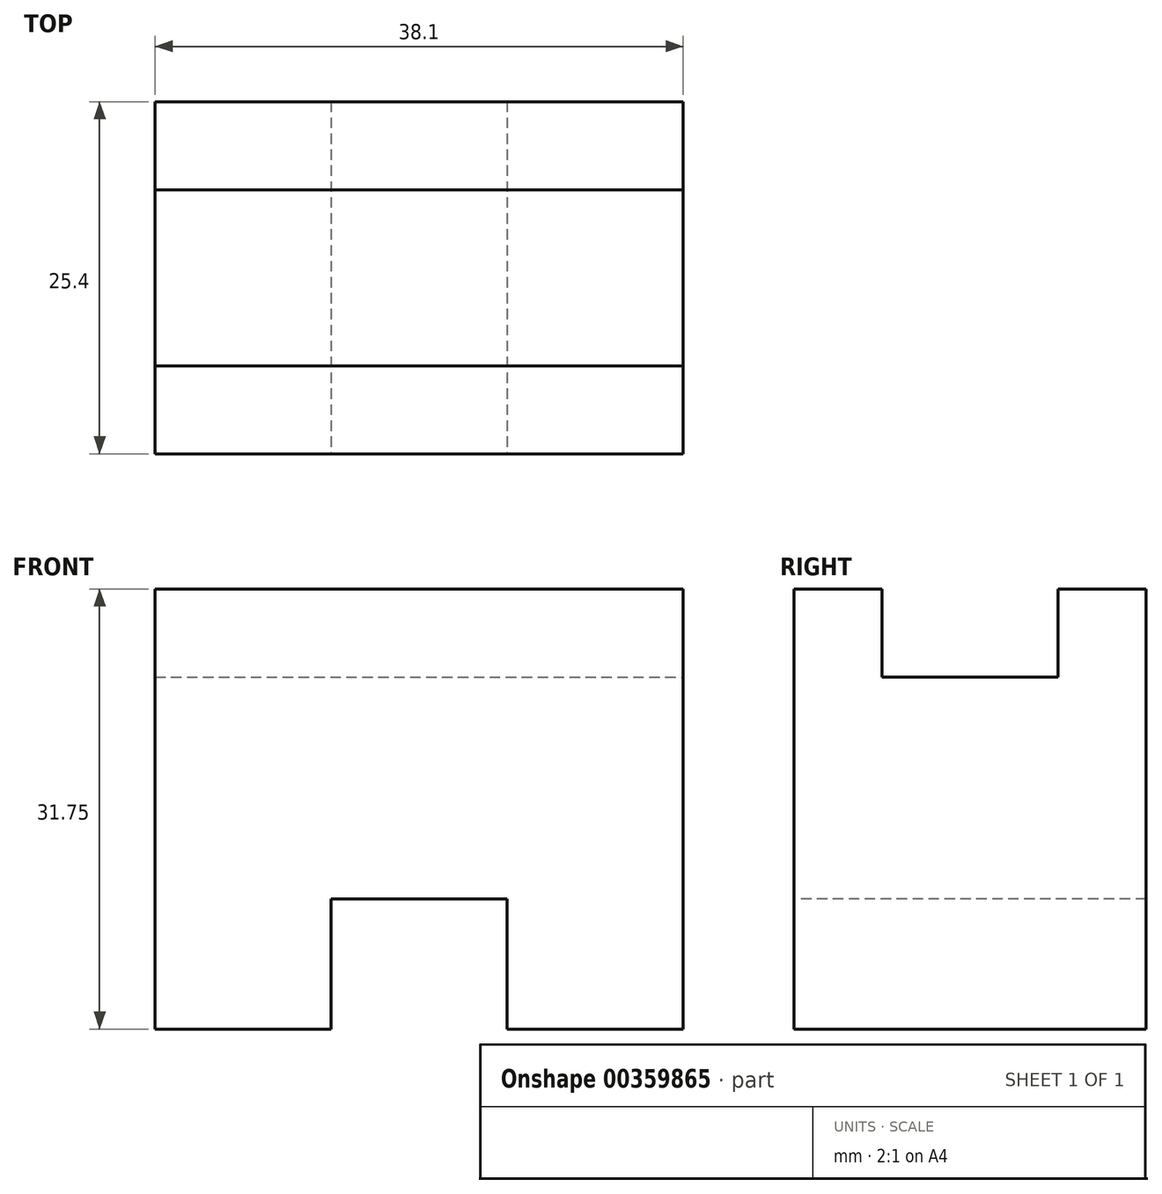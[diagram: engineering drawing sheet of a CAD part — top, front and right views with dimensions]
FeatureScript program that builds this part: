
annotation { "Feature Type Name" : "Feature", "Feature Type Description" : "" }
export const myFeature = defineFeature(function(context is Context, id is Id, definition is map)
    precondition{}
    {
        {
            var Q0;
            Q0=qCreatedBy(makeId("Front.planeOp"),FACE);
            var sketch = newSketch(context, id + "F0", { "sketchPlane" : qUnion([Q0])});
            skLineSegment(sketch, "E0", {"start": v(0, 0) * mm, "end": v(12.7, 0) * mm});
            skLineSegment(sketch, "E1", {"start": v(12.7, 0) * mm, "end": v(12.7, 9.4) * mm});
            skLineSegment(sketch, "E2", {"start": v(12.7, 9.4) * mm, "end": v(25.4, 9.4) * mm});
            skLineSegment(sketch, "E3", {"start": v(25.4, 9.4) * mm, "end": v(25.4, 0) * mm});
            skLineSegment(sketch, "E4", {"start": v(25.4, 0) * mm, "end": v(38.1, 0) * mm});
            skLineSegment(sketch, "E5", {"start": v(38.1, 0) * mm, "end": v(38.1, 31.75) * mm});
            skLineSegment(sketch, "E6", {"start": v(38.1, 31.75) * mm, "end": v(0, 31.75) * mm});
            skLineSegment(sketch, "E7", {"start": v(0, 31.75) * mm, "end": v(0, 0) * mm});
            skSolve(sketch);
        }
        {
            var Q0;
            Q0=makeQuery(id+"F0.imprint","IMPRINT",FACE,{"disambiguationData":[TD([[makeQuery(id+"F0.imprint","IMPRINT",EDGE,{"derivedFrom":sQuery(id+"F0.wireOp",EDGE,"E0")}),1.0]])]});
            extrude(context, id + "F1", {"entities" : qUnion([Q0]), "oppositeDirection" : true, "depth" : 25.4 * mm});
        }
        {
            var Q0;
            Q0=makeQuery(id+"F1.opExtrude","SWEPT_FACE",FACE,{"disambiguationData":[OSD([sQuery(id+"F0.wireOp",EDGE,"E5")])]});
            var sketch = newSketch(context, id + "F2", { "sketchPlane" : qUnion([Q0])});
            skLineSegment(sketch, "E8", {"start": v(6.35, 31.75) * mm, "end": v(6.35, 25.4) * mm});
            skLineSegment(sketch, "E9", {"start": v(6.35, 25.4) * mm, "end": v(19.05, 25.4) * mm});
            skLineSegment(sketch, "E10", {"start": v(19.05, 25.4) * mm, "end": v(19.05, 31.75) * mm});
            skLineSegment(sketch, "E11", {"start": v(19.05, 31.75) * mm, "end": v(6.35, 31.75) * mm});
            skSolve(sketch);
        }
        {
            var Q0;
            Q0=makeQuery(id+"F2.imprint","IMPRINT",FACE,{"disambiguationData":[TD([[makeQuery(id+"F2.imprint","IMPRINT",EDGE,{"derivedFrom":sQuery(id+"F2.wireOp",EDGE,"E8")}),1.0]])]});
            extrude(context, id + "F3", {"entities" : qUnion([Q0]), "operationType" : NewBodyOperationType.REMOVE, "oppositeDirection" : true, "depth" : 38.1 * mm});
        }
    });
